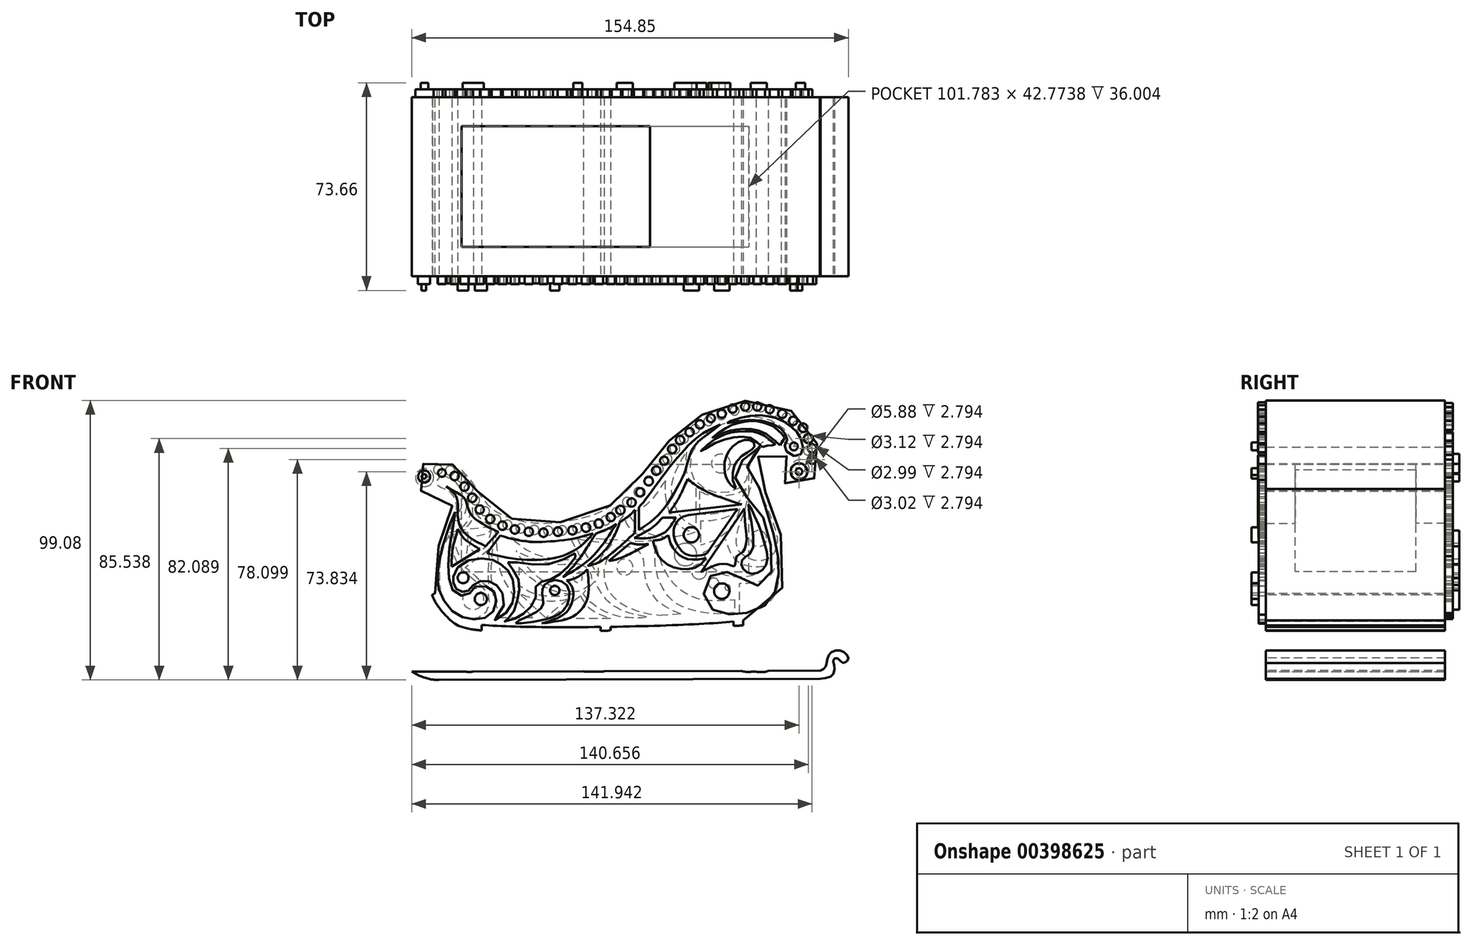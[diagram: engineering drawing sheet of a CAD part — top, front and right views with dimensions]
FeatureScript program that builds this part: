
annotation { "Feature Type Name" : "Feature", "Feature Type Description" : "" }
export const myFeature = defineFeature(function(context is Context, id is Id, definition is map)
    precondition{}
    {
        {
            var Q0;
            Q0=qCreatedBy(makeId("Front.planeOp"),FACE);
            var sketch = newSketch(context, id + "F0", { "sketchPlane" : qUnion([Q0])});
            skFitSpline(sketch, "E0", {"points": [v(-61.86, 0) * mm, v(-57.67, 0) * mm, v(-54.62, 0) * mm, v(-50.46, -2.56) * mm, v(-47.09, -6.88) * mm, v(-42.9, -13.1) * mm, v(-36.28, -18.14) * mm, v(-25.89, -20.79) * mm, v(-16.61, -20.62) * mm, v(-2.67, -17.38) * mm, v(3.41, -13.23) * mm, v(9.36, -7.64) * mm, v(15.85, 0) * mm, v(20.05, 5.35) * mm, v(25.4, 11.22) * mm, v(30.74, 15.47) * mm, v(37.88, 19.2) * mm, v(46.06, 21.92) * mm, v(55.6, 22.38) * mm, v(64.68, 19.42) * mm, v(70.58, 15.1) * mm, v(74.67, 8.3) * mm, v(75.96, 1.9) * mm, v(74.88, -3.16) * mm, v(72.79, -6.6) * mm, v(68.74, -8.77) * mm, v(63.8, -6.88) * mm, v(62.4, -3.74) * mm, v(63.54, 0) * mm, v(64.22, 2.85) * mm, v(61.07, 5.87) * mm, v(55.34, 4.34) * mm, v(53.55, 0) * mm, v(54.05, -3.2) * mm, v(57.42, -11.71) * mm, v(60.14, -18.73) * mm, v(63.09, -28.95) * mm, v(63.32, -41) * mm, v(58.78, -51.23) * mm, v(40.39, -56.22) * mm, v(-46.03, -56.8) * mm, v(-55.95, -53.28) * mm, v(-60.56, -45.22) * mm, v(-60.56, -34.78) * mm, v(-58.24, -26.54) * mm, v(-54.8, -18.71) * mm, v(-54.61, -13.18) * mm, v(-58.24, -9.36) * mm, v(-66.26, -9.17) * mm, v(-68.55, -3.06) * mm, v(-65.44, 0) * mm, v(-61.86, 0) * mm]});
            skSolve(sketch);
        }
        {
            var Q0;
            Q0 = qSketchRegion(id + "F0", true);
            extrude(context, id + "F1", {"entities" : qUnion([Q0]), "endBound" : BoundingType.SYMMETRIC, "oppositeDirection" : true, "depth" : 63.5 * mm});
        }
        {
            var Q0;
            Q0=makeQuery(id+"F1.opExtrude","CAP_FACE",FACE,{"disambiguationData":[OSD([sQuery(id+"F0.wireOp",EDGE,"E0")])],"isStart":true});
            var sketch = newSketch(context, id + "F2", { "sketchPlane" : qUnion([Q0])});
            skFitSpline(sketch, "E1.0.0", {"points": [v(-61.86, 0) * mm, v(-63.13, 0.1) * mm, v(-65.5, 0.56) * mm, v(-69.8, -2.61) * mm, v(-67.25, -11.56) * mm, v(-57.78, -7.7) * mm, v(-53.94, -13.18) * mm, v(-54.33, -18.98) * mm, v(-58.67, -26.6) * mm, v(-60.83, -34.68) * mm, v(-61.74, -45.34) * mm, v(-55.85, -54.48) * mm, v(-45.94, -58.76) * mm, v(40.55, -57.53) * mm, v(59.3, -53.74) * mm, v(64.17, -40.9) * mm, v(63.67, -29.06) * mm, v(60.18, -18.63) * mm, v(57.6, -12.08) * mm, v(53.88, -3.27) * mm, v(53.28, -0.14) * mm, v(54.58, 5.11) * mm, v(61.24, 7) * mm, v(64.98, 2.93) * mm, v(63.5, 0) * mm, v(61.9, -3.76) * mm, v(63.4, -7.3) * mm, v(68.85, -9.7) * mm, v(73.08, -6.78) * mm, v(75.06, -3.22) * mm, v(76.43, 2.03) * mm, v(75, 8.47) * mm, v(70.94, 15.58) * mm, v(64.8, 19.75) * mm, v(55.64, 23.08) * mm, v(45.99, 22.33) * mm, v(37.91, 19.4) * mm, v(30.6, 15.67) * mm, v(25.31, 11.43) * mm, v(19.88, 5.3) * mm, v(15.92, 0) * mm, v(9.53, -7.83) * mm, v(3.35, -13.28) * mm, v(-2.26, -18.21) * mm, v(-16.9, -20.96) * mm, v(-25.6, -21.2) * mm, v(-36.62, -18.82) * mm, v(-43.18, -13.54) * mm, v(-46.98, -6.86) * mm, v(-50.06, -2.48) * mm, v(-54.53, 0.48) * mm, v(-57.64, -0.1) * mm, v(-60.49, -0.12) * mm, v(-61.86, 0) * mm]});
            skLineSegment(sketch, "E2", {"start": v(-1.73, -57.73) * mm, "end": v(-1.73, -67.97) * mm});
            skLineSegment(sketch, "E3", {"start": v(1.77, -57.68) * mm, "end": v(1.77, -67.97) * mm});
            skFitSpline(sketch, "E4", {"points": [v(1.77, -67.97) * mm, v(1.77, -69.29) * mm, v(1.77, -70.2) * mm, v(1.57, -71.41) * mm, v(0.81, -72.5) * mm, v(-0.75, -73.5) * mm, v(-2.72, -73.58) * mm, v(-4.05, -73.54) * mm, v(-5.81, -73.54) * mm, v(-7.46, -73.54) * mm, v(-8.98, -72.54) * mm, v(-10.15, -70.73) * mm, v(-10.4, -68.5) * mm, v(-9.87, -67.4) * mm, v(-8.78, -66.52) * mm, v(-7.54, -66.03) * mm, v(-6.25, -66.03) * mm, v(-7.46, -67.2) * mm, v(-7.9, -69) * mm, v(-6.7, -70.45) * mm, v(-4.4, -70.85) * mm, v(-2.32, -70.09) * mm, v(-1.73, -67.97) * mm], "startDerivative": vector(-0.56, -33.67) * mm, "endDerivative": vector(1.72, 42.6) * mm});
            skLineSegment(sketch, "E5", {"start": v(45.37, -55.79) * mm, "end": v(45.37, -67.97) * mm});
            skLineSegment(sketch, "E6", {"start": v(48.81, -55.35) * mm, "end": v(48.81, -67.97) * mm});
            skFitSpline(sketch, "E7", {"points": [v(45.37, -67.97) * mm, v(45.37, -70.22) * mm, v(47.36, -72.86) * mm, v(50.54, -73.7) * mm, v(52.72, -73.58) * mm, v(56.1, -73.7) * mm, v(58.5, -72.7) * mm, v(59.86, -70.7) * mm, v(60.76, -67.97) * mm, v(60.93, -65.94) * mm, v(61.33, -64.67) * mm, v(63.14, -64.75) * mm, v(64.22, -66.01) * mm, v(63.8, -64.27) * mm, v(61.87, -63.62) * mm, v(60, -62.15) * mm, v(56.74, -62.03) * mm, v(56.33, -63.47) * mm, v(58.83, -64.44) * mm, v(59.51, -65.35) * mm, v(58.55, -69.4) * mm, v(56, -71.1) * mm, v(52.25, -71.03) * mm, v(49.75, -69.92) * mm, v(48.81, -67.97) * mm], "startDerivative": vector(-7.62, -66.67) * mm, "endDerivative": vector(-3.84, 62.66) * mm});
            skLineSegment(sketch, "E8", {"start": v(-47.46, -56.64) * mm, "end": v(-47.46, -68.5) * mm});
            skLineSegment(sketch, "E9", {"start": v(-43.88, -57) * mm, "end": v(-43.88, -68.5) * mm});
            skFitSpline(sketch, "E10", {"points": [v(-47.46, -68.5) * mm, v(-47.46, -69.9) * mm, v(-48.22, -71) * mm, v(-50.25, -71.71) * mm, v(-52.16, -71.53) * mm, v(-53.4, -70.46) * mm, v(-53.33, -68.77) * mm, v(-52.52, -67.63) * mm, v(-51.58, -66.61) * mm, v(-53.13, -66.75) * mm, v(-55.09, -68.5) * mm, v(-55.29, -71.2) * mm, v(-53.06, -73.36) * mm, v(-50.87, -73.58) * mm, v(-48.92, -73.64) * mm, v(-47.1, -73.58) * mm, v(-44.87, -72.3) * mm, v(-43.88, -68.5) * mm], "startDerivative": vector(0, -28.6) * mm, "endDerivative": vector(-5.76, 44.43) * mm});
            skLineSegment(sketch, "E11", {"start": v(76.25, -73.2) * mm, "end": v(-70.53, -73.58) * mm});
            skFitSpline(sketch, "E12", {"points": [v(-70.53, -73.58) * mm, v(-59.88, -73.36) * mm, v(-63.48, -72.42) * mm, v(-67.53, -70) * mm, v(-70.5, -66.08) * mm, v(-71.71, -60.54) * mm, v(-71.04, -55.27) * mm, v(-67.66, -50.41) * mm, v(-63.61, -47.44) * mm, v(-60.4, -45.82) * mm], "startDerivative": vector(-23.86, 1.15) * mm, "endDerivative": vector(29.7, 14.91) * mm});
            skFitSpline(sketch, "E13", {"points": [v(-60.99, -42.81) * mm, v(-62.8, -43.8) * mm, v(-64.8, -44.63) * mm, v(-66.96, -43.38) * mm, v(-69.12, -41.79) * mm, v(-73.18, -41.35) * mm, v(-74.11, -43.5) * mm, v(-71.95, -44.63) * mm, v(-69.69, -44.34) * mm, v(-67.75, -45.08) * mm, v(-66.85, -46.5) * mm, v(-70.7, -49.74) * mm, v(-74.68, -56.32) * mm, v(-74.68, -63.14) * mm, v(-73.66, -67.34) * mm, v(-71.27, -71.31) * mm, v(-66.58, -74.72) * mm, v(-61.59, -76.34) * mm, v(-59.02, -76.45) * mm], "startDerivative": vector(-40.03, -24.4) * mm, "endDerivative": vector(48.56, 3.48) * mm});
            skLineSegment(sketch, "E14", {"start": v(-59.02, -76.45) * mm, "end": v(76.08, -76.1) * mm});
            skFitSpline(sketch, "E15", {"points": [v(76.25, -73.2) * mm, v(77.38, -72.61) * mm, v(78.23, -71.53) * mm, v(78.52, -70.34) * mm, v(78.91, -68.4) * mm, v(79.7, -67.1) * mm, v(81.64, -66.08) * mm, v(83.92, -66.36) * mm, v(85.45, -67.38) * mm, v(86.13, -68.7) * mm, v(85.5, -70.06) * mm, v(84.09, -70.45) * mm, v(82.95, -69.49) * mm, v(82.04, -68.75) * mm, v(81, -69.06) * mm, v(80.8, -70.44) * mm, v(81.2, -71.89) * mm, v(80.88, -74.32) * mm, v(79.31, -75.51) * mm, v(76.08, -76.1) * mm], "startDerivative": vector(25.22, 10.43) * mm, "endDerivative": vector(-46.19, -6.72) * mm});
            skSolve(sketch);
        }
        {
            var Q0;
            {var subQ1=sQuery(id+"F2.wireOp",EDGE,"E5");Q0=makeQuery(id+"F2.imprint","IMPRINT",FACE,{"disambiguationData":[TD([[makeQuery(id+"F2.imprint","IMPRINT",EDGE,{"derivedFrom":subQ1}),1.0]])]});}
            var Q1;
            {var subQ4=sQuery(id+"F2.wireOp",EDGE,"E2");Q1=makeQuery(id+"F2.imprint","IMPRINT",FACE,{"disambiguationData":[TD([[makeQuery(id+"F2.imprint","IMPRINT",EDGE,{"derivedFrom":subQ4}),1.0]])]});}
            var Q2;
            {var subQ1=sQuery(id+"F2.wireOp",EDGE,"E8");Q2=makeQuery(id+"F2.imprint","IMPRINT",FACE,{"disambiguationData":[TD([[makeQuery(id+"F2.imprint","IMPRINT",EDGE,{"derivedFrom":subQ1}),1.0]])]});}
            var Q3;
            {var subQ11=sQuery(id+"F2.wireOp",EDGE,"E14");Q3=makeQuery(id+"F2.imprint","IMPRINT",FACE,{"disambiguationData":[TD([[makeQuery(id+"F2.imprint","IMPRINT",EDGE,{"derivedFrom":subQ11}),1.0]])]});}
            var Q4;
            {var subQ0=sQuery(id+"F2.wireOp",EDGE,"E12");var subQ1=sQuery(id+"F2.wireOp",EDGE,"E1.0.0");var subQ2=makeQuery(id+"F2.imprint","INTERSECT",VERTEX,{"derivedFrom":[subQ1,subQ0]});Q4=makeQuery(id+"F2.imprint","IMPRINT",FACE,{"disambiguationData":[TD([[makeQuery(id+"F2.imprint","IMPRINT",EDGE,{"disambiguationData":[TD([[subQ2,-1.0]])],"derivedFrom":subQ1}),1.0]])]});}
            extrude(context, id + "F3", {"entities" : qUnion([Q0, Q1, Q2, Q3, Q4]), "operationType" : NewBodyOperationType.ADD, "oppositeDirection" : true, "depth" : 63.5 * mm});
        }
        {
            var Q0;
            {var subQ0=sQuery(id+"F2.wireOp",EDGE,"E1.0.0");var subQ1=sQuery(id+"F2.wireOp",EDGE,"E11");Q0=makeQuery(id+"F3.boolean.opBoolean","MERGE",FACE,{"derivedFrom":[makeQuery(id+"F1.opExtrude","CAP_FACE",FACE,{"disambiguationData":[OSD([sQuery(id+"F0.wireOp",EDGE,"E0")])],"isStart":true}),makeQuery(id+"F3.opExtrude","CAP_FACE",FACE,{"disambiguationData":[OSD([subQ0,sQuery(id+"F2.wireOp",EDGE,"E5"),sQuery(id+"F2.wireOp",EDGE,"E6"),sQuery(id+"F2.wireOp",EDGE,"E7"),subQ1])],"isStart":true}),makeQuery(id+"F3.opExtrude","CAP_FACE",FACE,{"disambiguationData":[OSD([subQ0,sQuery(id+"F2.wireOp",EDGE,"E2"),sQuery(id+"F2.wireOp",EDGE,"E3"),sQuery(id+"F2.wireOp",EDGE,"E4"),subQ1])],"isStart":true}),makeQuery(id+"F3.opExtrude","CAP_FACE",FACE,{"disambiguationData":[OSD([subQ0,sQuery(id+"F2.wireOp",EDGE,"E8"),sQuery(id+"F2.wireOp",EDGE,"E9"),sQuery(id+"F2.wireOp",EDGE,"E10"),subQ1])],"isStart":true}),makeQuery(id+"F3.opExtrude","CAP_FACE",FACE,{"disambiguationData":[OSD([subQ0,sQuery(id+"F2.wireOp",EDGE,"E12"),sQuery(id+"F2.wireOp",EDGE,"E13")])],"isStart":true})]});}
            var sketch = newSketch(context, id + "F4", { "sketchPlane" : qUnion([Q0])});
            skCircle(sketch, "E16", {"center": v(-64.26, -4.42) * mm, "radius": 2.16 * mm});
            skCircle(sketch, "E17", {"center": v(68.61, -2.65) * mm, "radius": 2.96 * mm});
            skCircle(sketch, "E18", {"center": v(-57.99, -3.13) * mm, "radius": 1.37 * mm});
            skCircle(sketch, "E19", {"center": v(-49.97, -7.96) * mm, "radius": 1.52 * mm});
            skCircle(sketch, "E20", {"center": v(-47.2, -11.95) * mm, "radius": 1.52 * mm});
            skCircle(sketch, "E21", {"center": v(-53.47, -4.2) * mm, "radius": 1.51 * mm});
            skCircle(sketch, "E22", {"center": v(-44.56, -16.07) * mm, "radius": 1.5 * mm});
            skCircle(sketch, "E23", {"center": v(-40.84, -19.45) * mm, "radius": 1.5 * mm});
            skCircle(sketch, "E24", {"center": v(-36.51, -21.82) * mm, "radius": 1.51 * mm});
            skCircle(sketch, "E25", {"center": v(-32.1, -23.17) * mm, "radius": 1.5 * mm});
            skCircle(sketch, "E26", {"center": v(-27.17, -23.98) * mm, "radius": 1.5 * mm});
            skCircle(sketch, "E27", {"center": v(-21.95, -24.31) * mm, "radius": 1.5 * mm});
            skCircle(sketch, "E28", {"center": v(-16.84, -23.93) * mm, "radius": 1.51 * mm});
            skCircle(sketch, "E29", {"center": v(-11.67, -23.45) * mm, "radius": 1.5 * mm});
            skCircle(sketch, "E30", {"center": v(-6.9, -22.5) * mm, "radius": 1.51 * mm});
            skCircle(sketch, "E31", {"center": v(-2.38, -21.09) * mm, "radius": 1.5 * mm});
            skCircle(sketch, "E32", {"center": v(1.88, -18.77) * mm, "radius": 1.49 * mm});
            skCircle(sketch, "E33", {"center": v(5.32, -16.28) * mm, "radius": 1.53 * mm});
            skCircle(sketch, "E34", {"center": v(9.3, -13.6) * mm, "radius": 1.49 * mm});
            skCircle(sketch, "E35", {"center": v(12.35, -9.97) * mm, "radius": 1.5 * mm});
            skCircle(sketch, "E36", {"center": v(15.34, -6.05) * mm, "radius": 1.5 * mm});
            skCircle(sketch, "E37", {"center": v(18, -2.3) * mm, "radius": 1.51 * mm});
            skCircle(sketch, "E38", {"center": v(20.81, 1.23) * mm, "radius": 1.46 * mm});
            skCircle(sketch, "E39", {"center": v(23.66, 5.32) * mm, "radius": 1.5 * mm});
            skCircle(sketch, "E40", {"center": v(26.49, 8.56) * mm, "radius": 1.51 * mm});
            skCircle(sketch, "E41", {"center": v(29.82, 11.34) * mm, "radius": 1.49 * mm});
            skCircle(sketch, "E42", {"center": v(33.46, 14.13) * mm, "radius": 1.49 * mm});
            skCircle(sketch, "E43", {"center": v(37.39, 16.3) * mm, "radius": 1.45 * mm});
            skCircle(sketch, "E44", {"center": v(41.24, 17.92) * mm, "radius": 1.48 * mm});
            skCircle(sketch, "E45", {"center": v(45.1, 19.68) * mm, "radius": 1.49 * mm});
            skCircle(sketch, "E46", {"center": v(49.56, 20.42) * mm, "radius": 1.48 * mm});
            skCircle(sketch, "E47", {"center": v(53.82, 20.42) * mm, "radius": 1.46 * mm});
            skCircle(sketch, "E48", {"center": v(58.22, 19.47) * mm, "radius": 1.45 * mm});
            skCircle(sketch, "E49", {"center": v(62.68, 17.85) * mm, "radius": 1.5 * mm});
            skCircle(sketch, "E50", {"center": v(66.54, 15.35) * mm, "radius": 1.5 * mm});
            skCircle(sketch, "E51", {"center": v(70.05, 12.91) * mm, "radius": 1.51 * mm});
            skCircle(sketch, "E52", {"center": v(71.95, 9.06) * mm, "radius": 1.56 * mm});
            skCircle(sketch, "E53", {"center": v(73.23, 5.6) * mm, "radius": 1.5 * mm});
            skCircle(sketch, "E54", {"center": v(73.23, 1.62) * mm, "radius": 1.51 * mm});
            skCircle(sketch, "E55", {"center": v(68.61, -2.65) * mm, "radius": 2.94 * mm});
            skCircle(sketch, "E56", {"center": v(73.23, 1.62) * mm, "radius": 1.52 * mm});
            skCircle(sketch, "E57", {"center": v(71.95, 9.06) * mm, "radius": 1.65 * mm});
            skSolve(sketch);
        }
        {
            var Q0;
            Q0 = qSketchRegion(id + "F4", true);
            extrude(context, id + "F5", {"entities" : qUnion([Q0]), "operationType" : NewBodyOperationType.ADD, "depth" : 2.8 * mm});
        }
        {
            var Q0;
            {var subQ0=sQuery(id+"F2.wireOp",EDGE,"E1.0.0");var subQ1=sQuery(id+"F2.wireOp",EDGE,"E11");Q0=makeQuery(id+"F3.boolean.opBoolean","MERGE",FACE,{"derivedFrom":[makeQuery(id+"F1.opExtrude","CAP_FACE",FACE,{"disambiguationData":[OSD([sQuery(id+"F0.wireOp",EDGE,"E0")])],"isStart":false}),makeQuery(id+"F3.opExtrude","CAP_FACE",FACE,{"disambiguationData":[OSD([subQ0,sQuery(id+"F2.wireOp",EDGE,"E5"),sQuery(id+"F2.wireOp",EDGE,"E6"),sQuery(id+"F2.wireOp",EDGE,"E7"),subQ1])],"isStart":false}),makeQuery(id+"F3.opExtrude","CAP_FACE",FACE,{"disambiguationData":[OSD([subQ0,sQuery(id+"F2.wireOp",EDGE,"E2"),sQuery(id+"F2.wireOp",EDGE,"E3"),sQuery(id+"F2.wireOp",EDGE,"E4"),subQ1])],"isStart":false}),makeQuery(id+"F3.opExtrude","CAP_FACE",FACE,{"disambiguationData":[OSD([subQ0,sQuery(id+"F2.wireOp",EDGE,"E8"),sQuery(id+"F2.wireOp",EDGE,"E9"),sQuery(id+"F2.wireOp",EDGE,"E10"),subQ1])],"isStart":false}),makeQuery(id+"F3.opExtrude","CAP_FACE",FACE,{"disambiguationData":[OSD([subQ0,sQuery(id+"F2.wireOp",EDGE,"E12"),sQuery(id+"F2.wireOp",EDGE,"E13")])],"isStart":false})]});}
            var sketch = newSketch(context, id + "F6", { "sketchPlane" : qUnion([Q0])});
            skCircle(sketch, "E58", {"center": v(-69, -1.6) * mm, "radius": 3.2 * mm});
            skCircle(sketch, "E59", {"center": v(-71.78, 4.77) * mm, "radius": 1.56 * mm});
            skCircle(sketch, "E60", {"center": v(-70.35, 9.74) * mm, "radius": 1.54 * mm});
            skCircle(sketch, "E61", {"center": v(-67.86, 13.71) * mm, "radius": 1.56 * mm});
            skCircle(sketch, "E62", {"center": v(-64.22, 16.58) * mm, "radius": 1.56 * mm});
            skCircle(sketch, "E63", {"center": v(-59.78, 18.5) * mm, "radius": 1.6 * mm});
            skCircle(sketch, "E64", {"center": v(-55.09, 20.12) * mm, "radius": 1.53 * mm});
            skCircle(sketch, "E65", {"center": v(-50.55, 20.07) * mm, "radius": 1.56 * mm});
            skCircle(sketch, "E66", {"center": v(-45.81, 18.97) * mm, "radius": 1.58 * mm});
            skCircle(sketch, "E67", {"center": v(-41.09, 17.35) * mm, "radius": 1.57 * mm});
            skCircle(sketch, "E68", {"center": v(-36.48, 15.22) * mm, "radius": 1.57 * mm});
            skCircle(sketch, "E69", {"center": v(-31.81, 12.48) * mm, "radius": 1.58 * mm});
            skCircle(sketch, "E70", {"center": v(-27.83, 9.07) * mm, "radius": 1.58 * mm});
            skCircle(sketch, "E71", {"center": v(-24.65, 5.45) * mm, "radius": 1.76 * mm});
            skCircle(sketch, "E72", {"center": v(-21.94, 1.9) * mm, "radius": 1.67 * mm});
            skCircle(sketch, "E73", {"center": v(-18.83, -1.75) * mm, "radius": 1.68 * mm});
            skCircle(sketch, "E74", {"center": v(-15.37, -5.83) * mm, "radius": 1.65 * mm});
            skCircle(sketch, "E75", {"center": v(-11.72, -9.89) * mm, "radius": 1.63 * mm});
            skCircle(sketch, "E76", {"center": v(-7.66, -13.4) * mm, "radius": 1.63 * mm});
            skCircle(sketch, "E77", {"center": v(-3.87, -17.06) * mm, "radius": 1.6 * mm});
            skCircle(sketch, "E78", {"center": v(0, -19.96) * mm, "radius": 1.63 * mm});
            skCircle(sketch, "E79", {"center": v(4.71, -21.79) * mm, "radius": 1.59 * mm});
            skCircle(sketch, "E80", {"center": v(9.99, -22.73) * mm, "radius": 1.62 * mm});
            skCircle(sketch, "E81", {"center": v(15.33, -23.48) * mm, "radius": 1.67 * mm});
            skCircle(sketch, "E82", {"center": v(20.27, -23.62) * mm, "radius": 1.63 * mm});
            skCircle(sketch, "E83", {"center": v(25.25, -23.33) * mm, "radius": 1.64 * mm});
            skCircle(sketch, "E84", {"center": v(30.05, -22.8) * mm, "radius": 1.62 * mm});
            skCircle(sketch, "E85", {"center": v(34.72, -21.49) * mm, "radius": 1.62 * mm});
            skCircle(sketch, "E86", {"center": v(38.7, -19.67) * mm, "radius": 1.65 * mm});
            skCircle(sketch, "E87", {"center": v(42.69, -16.71) * mm, "radius": 1.59 * mm});
            skCircle(sketch, "E88", {"center": v(46.15, -12.79) * mm, "radius": 1.58 * mm});
            skCircle(sketch, "E89", {"center": v(48.54, -8.75) * mm, "radius": 1.6 * mm});
            skCircle(sketch, "E90", {"center": v(51.04, -4.76) * mm, "radius": 1.64 * mm});
            skCircle(sketch, "E91", {"center": v(55.1, -2.3) * mm, "radius": 1.65 * mm});
            skCircle(sketch, "E92", {"center": v(64.11, -4.78) * mm, "radius": 3.2 * mm});
            skCircle(sketch, "E93", {"center": v(59.35, -1.94) * mm, "radius": 1.6 * mm});
            skSolve(sketch);
        }
        {
            var Q0;
            Q0 = qSketchRegion(id + "F6", true);
            extrude(context, id + "F7", {"entities" : qUnion([Q0]), "operationType" : NewBodyOperationType.ADD, "depth" : 2.8 * mm});
        }
        {
            var Q0;
            {var subQ0=sQuery(id+"F2.wireOp",EDGE,"E6");var subQ1=sQuery(id+"F2.wireOp",EDGE,"E5");var subQ2=sQuery(id+"F0.wireOp",EDGE,"E0");var subQ3=sQuery(id+"F2.wireOp",EDGE,"E12");var subQ4=sQuery(id+"F2.wireOp",EDGE,"E4");var subQ5=sQuery(id+"F2.wireOp",EDGE,"E2");var subQ6=sQuery(id+"F2.wireOp",EDGE,"E11");var subQ8=sQuery(id+"F2.wireOp",EDGE,"E7");var subQ11=sQuery(id+"F2.wireOp",EDGE,"E8");var subQ12=sQuery(id+"F2.wireOp",EDGE,"E3");var subQ14=sQuery(id+"F2.wireOp",EDGE,"E13");var subQ15=sQuery(id+"F2.wireOp",EDGE,"E1.0.0");var subQ16=sQuery(id+"F2.wireOp",EDGE,"E9");var subQ17=sQuery(id+"F2.wireOp",EDGE,"E10");Q0=makeQuery(id+"F5.boolean.opBoolean","SPLIT",FACE,{"disambiguationData":[TD([makeQuery(id+"F1.opExtrude","SWEPT_FACE",FACE,{"disambiguationData":[OSD([subQ2])]})])],"derivedFrom":makeQuery(id+"F3.boolean.opBoolean","MERGE",FACE,{"derivedFrom":[makeQuery(id+"F1.opExtrude","CAP_FACE",FACE,{"disambiguationData":[OSD([subQ2])],"isStart":true}),makeQuery(id+"F3.opExtrude","CAP_FACE",FACE,{"disambiguationData":[OSD([subQ15,subQ1,subQ0,subQ8,subQ6])],"isStart":true}),makeQuery(id+"F3.opExtrude","CAP_FACE",FACE,{"disambiguationData":[OSD([subQ15,subQ5,subQ12,subQ4,subQ6])],"isStart":true}),makeQuery(id+"F3.opExtrude","CAP_FACE",FACE,{"disambiguationData":[OSD([subQ15,subQ11,subQ16,subQ17,subQ6])],"isStart":true}),makeQuery(id+"F3.opExtrude","CAP_FACE",FACE,{"disambiguationData":[OSD([subQ15,subQ3,subQ14])],"isStart":true})]})});}
            var sketch = newSketch(context, id + "F8", { "sketchPlane" : qUnion([Q0])});
            skFitSpline(sketch, "E94", {"points": [v(-56.44, -7.86) * mm, v(-50.71, -11.36) * mm, v(-49.16, -13.95) * mm, v(-47.8, -17.67) * mm, v(-44.9, -20.24) * mm, v(-41.28, -22.44) * mm, v(-37.95, -24) * mm], "startDerivative": vector(17.34, -13.46) * mm, "endDerivative": vector(19.44, -9.17) * mm});
            skLineSegment(sketch, "E95", {"start": v(-37.95, -24) * mm, "end": v(-42.47, -29.1) * mm});
            skFitSpline(sketch, "E96", {"points": [v(-56.44, -7.86) * mm, v(-53.05, -11.19) * mm, v(-52.3, -14.57) * mm, v(-52.36, -17.55) * mm, v(-51.96, -20.88) * mm, v(-49.2, -25.09) * mm, v(-42.47, -29.1) * mm], "startDerivative": vector(21.25, -16.5) * mm, "endDerivative": vector(32.89, -15.83) * mm});
            skFitSpline(sketch, "E97", {"points": [v(-53.23, -16.99) * mm, v(-57.76, -29.02) * mm, v(-59.45, -38.3) * mm, v(-59.25, -43.57) * mm, v(-56.64, -49.3) * mm, v(-52.45, -53.5) * mm, v(-47.58, -54.98) * mm, v(-42.98, -54.58) * mm, v(-39.82, -52.32) * mm, v(-38.67, -48.11) * mm, v(-39.62, -45.05) * mm, v(-42.97, -43.14) * mm, v(-46.7, -43.8) * mm, v(-48.23, -46) * mm, v(-51, -46.58) * mm, v(-54.45, -44.28) * mm, v(-55.56, -38.48) * mm, v(-55.26, -28.89) * mm, v(-53.23, -16.99) * mm]});
            skFitSpline(sketch, "E98", {"points": [v(-52.34, -23) * mm, v(-53.93, -28.83) * mm, v(-54.5, -34.28) * mm, v(-54.5, -36.39) * mm], "startDerivative": vector(-2.88, -14.57) * mm, "endDerivative": vector(0.26, -7.92) * mm});
            skLineSegment(sketch, "E99", {"start": v(-54.5, -36.39) * mm, "end": v(-44.56, -30.17) * mm});
            skFitSpline(sketch, "E100", {"points": [v(-52.34, -23) * mm, v(-50.49, -25.96) * mm, v(-47.81, -28.16) * mm, v(-44.56, -30.17) * mm], "startDerivative": vector(6.82, -9.23) * mm, "endDerivative": vector(9.87, -5.81) * mm});
            skFitSpline(sketch, "E101", {"points": [v(-52.34, -36.67) * mm, v(-53.88, -39.74) * mm, v(-53.99, -40.68) * mm, v(-53.96, -42.02) * mm, v(-53.3, -43.72) * mm, v(-52.17, -44.7) * mm, v(-50.86, -45.29) * mm, v(-49.61, -45.26) * mm, v(-48.47, -44.72) * mm, v(-47.5, -43.52) * mm, v(-45.7, -41.95) * mm, v(-43.34, -41.34) * mm, v(-40.9, -41.68) * mm, v(-38.74, -42.81) * mm, v(-37, -44.78) * mm, v(-35.94, -49.37) * mm, v(-38.08, -53.27) * mm, v(-39.7, -55.3) * mm, v(-36.18, -53.54) * mm, v(-33.2, -49.75) * mm, v(-32.4, -45.96) * mm, v(-32.8, -40.96) * mm, v(-34.57, -37.58) * mm, v(-36.78, -35.66) * mm, v(-38.95, -34.37) * mm, v(-42.47, -33.52) * mm, v(-47.4, -33.77) * mm, v(-52.34, -36.67) * mm]});
            skLineSegment(sketch, "E102", {"start": v(-37.26, -25.33) * mm, "end": v(-41.92, -31.53) * mm});
            skFitSpline(sketch, "E103", {"points": [v(-37.26, -25.33) * mm, v(-34.99, -26.03) * mm, v(-31.02, -26.94) * mm, v(-25.62, -27.61) * mm, v(-19.92, -27.42) * mm, v(-12.94, -26.7) * mm, v(-4.43, -24.6) * mm], "startDerivative": vector(19.1, -6.34) * mm, "endDerivative": vector(40.6, 11.48) * mm});
            skFitSpline(sketch, "E104", {"points": [v(-41.92, -31.53) * mm, v(-33.41, -33.35) * mm, v(-25.04, -33.97) * mm, v(-15.86, -32.73) * mm, v(-9.02, -29.24) * mm, v(-4.43, -24.6) * mm], "startDerivative": vector(40.97, -10.8) * mm, "endDerivative": vector(23.23, 27.39) * mm});
            skFitSpline(sketch, "E105", {"points": [v(-34.57, -34.9) * mm, v(-32.02, -38.52) * mm, v(-30.5, -43.97) * mm, v(-31.64, -49.7) * mm, v(-33.84, -54.2) * mm, v(-36.04, -55.83) * mm, v(-31.83, -54.7) * mm, v(-27.9, -52) * mm, v(-24.75, -47.7) * mm, v(-24.48, -42.88) * mm, v(-21.21, -41.39) * mm, v(-16.83, -39.53) * mm, v(-12.24, -35.13) * mm, v(-10.21, -31.63) * mm, v(-16.14, -34.3) * mm, v(-27.07, -35.42) * mm, v(-34.57, -34.9) * mm]});
            skFitSpline(sketch, "E106", {"points": [v(-31.83, -56.37) * mm, v(-26.05, -53.26) * mm, v(-22.23, -50.1) * mm, v(-22.26, -47.04) * mm, v(-22.4, -44.74) * mm, v(-21.23, -42.45) * mm, v(-17.2, -41.11) * mm, v(-13.22, -43.73) * mm, v(-13.34, -49.34) * mm, v(-15.77, -52.58) * mm, v(-19.94, -54.7) * mm, v(-31.83, -56.37) * mm]});
            skFitSpline(sketch, "E107", {"points": [v(-15.06, -40.04) * mm, v(-9.83, -34.35) * mm, v(-6.7, -29.86) * mm, v(-3.46, -24.68) * mm], "startDerivative": vector(15.46, 15.9) * mm, "endDerivative": vector(10.16, 16.32) * mm});
            skFitSpline(sketch, "E108", {"points": [v(-3.46, -24.68) * mm, v(-1.24, -23.77) * mm, v(1.6, -22.58) * mm, v(3.88, -21.16) * mm], "startDerivative": vector(6.77, 2.85) * mm, "endDerivative": vector(6.5, 4.5) * mm});
            skFitSpline(sketch, "E109", {"points": [v(3.88, -21.16) * mm, v(-4.76, -32.93) * mm, v(-15.06, -40.04) * mm], "startDerivative": vector(-15.4, -24.71) * mm, "endDerivative": vector(-22.56, -12.9) * mm});
            skFitSpline(sketch, "E110", {"points": [v(-22.59, -56.49) * mm, v(-17.23, -54.72) * mm, v(-13.55, -52.13) * mm, v(-11.54, -47.83) * mm, v(-11.73, -44) * mm, v(-13.02, -41.8) * mm, v(-13.79, -41.28) * mm], "startDerivative": vector(26.39, 7.47) * mm, "endDerivative": vector(-8.58, 4.5) * mm});
            skFitSpline(sketch, "E111", {"points": [v(-13.79, -41.28) * mm, v(-11.2, -40.66) * mm, v(-7.86, -38.7) * mm, v(-6.47, -37.3) * mm], "startDerivative": vector(7.53, 1.15) * mm, "endDerivative": vector(4.12, 4.76) * mm});
            skFitSpline(sketch, "E112", {"points": [v(-6.47, -37.3) * mm, v(-6.04, -40.6) * mm, v(-6.04, -45.72) * mm, v(-6.95, -49.26) * mm, v(-9.63, -52.66) * mm, v(-13.54, -54.86) * mm, v(-22.59, -56.49) * mm], "startDerivative": vector(3.28, -22.1) * mm, "endDerivative": vector(-43.28, -5.66) * mm});
            skFitSpline(sketch, "E113", {"points": [v(54.82, 6.19) * mm, v(50.23, -0.7) * mm, v(54.25, -7.97) * mm, v(57.14, -16.25) * mm, v(59.44, -24.23) * mm, v(60.92, -31.13) * mm, v(61.46, -36.14) * mm, v(61.2, -40.74) * mm, v(60.11, -45.2) * mm, v(58.22, -48.58) * mm, v(53.62, -51.7) * mm, v(48.61, -53.05) * mm, v(44.42, -53.32) * mm, v(40.36, -52.5) * mm, v(36.55, -50.53) * mm, v(34.83, -45.18) * mm, v(36.74, -40.1) * mm, v(41.14, -38.3) * mm, v(44.2, -38.39) * mm, v(47.53, -39.8) * mm, v(51.18, -42.9) * mm, v(56.45, -41.92) * mm, v(59.22, -36.47) * mm, v(57.88, -25.38) * mm, v(53.86, -15.43) * mm, v(47.65, -9.21) * mm, v(46.02, -2.7) * mm, v(49.43, 2.14) * mm, v(54.82, 6.19) * mm]});
            skFitSpline(sketch, "E114", {"points": [v(66.85, 2.92) * mm, v(69.36, 3.67) * mm, v(70.05, 6.65) * mm, v(68.5, 10.5) * mm, v(66.68, 12.5) * mm, v(63.23, 15.16) * mm, v(59.45, 16.6) * mm, v(56.05, 17.27) * mm, v(51, 17.1) * mm, v(46.12, 15.85) * mm, v(43.06, 14.6) * mm, v(48.13, 15.37) * mm, v(55.29, 15.45) * mm, v(61.61, 13.07) * mm, v(63.43, 11.16) * mm, v(64.48, 9.15) * mm, v(63.7, 7) * mm, v(63.8, 5.08) * mm, v(66.85, 2.92) * mm]});
            skLineSegment(sketch, "E115", {"start": v(63.54, 9.39) * mm, "end": v(61.93, 6.73) * mm});
            skFitSpline(sketch, "E116", {"points": [v(63.54, 9.39) * mm, v(62.09, 11.16) * mm, v(59.63, 13.26) * mm, v(57.67, 14.17) * mm, v(54.45, 15.05) * mm, v(51.04, 15.28) * mm, v(46.5, 14.48) * mm, v(42.65, 12.75) * mm, v(37.96, 9.39) * mm, v(41.46, 10.93) * mm, v(45.76, 12.2) * mm, v(50.67, 12.53) * mm, v(55.9, 11.32) * mm, v(61.93, 6.73) * mm], "startDerivative": vector(-21.37, 30.93) * mm, "endDerivative": vector(57.36, -51.2) * mm});
            skFitSpline(sketch, "E117", {"points": [v(55.74, 6) * mm, v(57.12, 6.48) * mm, v(58.94, 6.77) * mm, v(60.33, 6.72) * mm, v(58.37, 8.59) * mm, v(56.55, 9.97) * mm, v(53.68, 11.22) * mm, v(51, 11.7) * mm, v(47.32, 11.6) * mm, v(44.54, 11.27) * mm, v(42.14, 10.5) * mm, v(40.01, 9.48) * mm, v(37.61, 8.06) * mm, v(33.83, 4.57) * mm, v(37.47, 6.72) * mm, v(43.7, 9.17) * mm, v(48.8, 9.69) * mm, v(52.68, 8.68) * mm, v(55.74, 6) * mm]});
            skFitSpline(sketch, "E118", {"points": [v(51.03, 8.57) * mm, v(52.5, 7.77) * mm, v(52.85, 6.24) * mm, v(52, 5.21) * mm, v(49.5, 3.68) * mm, v(46.65, 1.12) * mm, v(45.34, -1.72) * mm, v(45.34, -6.39) * mm, v(46.3, -8.78) * mm, v(45.11, -7.92) * mm, v(43.92, -6.84) * mm, v(43.12, -5.42) * mm, v(42.44, -3.72) * mm, v(42.21, -1.38) * mm, v(42.38, 1.35) * mm, v(43.46, 4.13) * mm, v(45.4, 6.58) * mm, v(48.92, 8.57) * mm, v(51.03, 8.57) * mm]});
            skFitSpline(sketch, "E119", {"points": [v(45.47, 8.2) * mm, v(43.27, 6.28) * mm, v(41.36, 2.55) * mm, v(40.88, -2.7) * mm, v(42.12, -6.91) * mm, v(45.66, -10.26) * mm, v(48.05, -11.41) * mm], "startDerivative": vector(-16.05, -11.76) * mm, "endDerivative": vector(16.58, -6.5) * mm});
            skFitSpline(sketch, "E120", {"points": [v(45.28, 8.2) * mm, v(42.12, 7.72) * mm, v(38.72, 6.46) * mm, v(34.47, 3.9) * mm, v(31.31, 1.4) * mm, v(30.2, -2.88) * mm, v(48.05, -11.41) * mm], "startDerivative": vector(-26, -1.56) * mm, "endDerivative": vector(91, -32.87) * mm});
            skFitSpline(sketch, "E121", {"points": [v(40.65, 14.04) * mm, v(33.83, 10.4) * mm, v(28.14, 5.29) * mm, v(21.1, -3.25) * mm, v(14.72, -11.9) * mm, v(11.88, -15.3) * mm], "startDerivative": vector(-36.56, -17.17) * mm, "endDerivative": vector(-17.61, -20.07) * mm});
            skLineSegment(sketch, "E122", {"start": v(11.88, -15.3) * mm, "end": v(11.88, -23.38) * mm});
            skFitSpline(sketch, "E123", {"points": [v(11.88, -23.38) * mm, v(19.04, -17.8) * mm, v(24.73, -9.62) * mm, v(28.03, -3.13) * mm, v(29.4, 1.76) * mm, v(32.34, 7.38) * mm, v(40.65, 14.04) * mm], "startDerivative": vector(42.16, 27.67) * mm, "endDerivative": vector(43.8, 40.17) * mm});
            skFitSpline(sketch, "E124", {"points": [v(29.14, -5.3) * mm, v(25.6, -12.7) * mm, v(22.54, -17.2) * mm], "startDerivative": vector(-6.32, -14.36) * mm, "endDerivative": vector(-6.9, -9.27) * mm});
            skLineSegment(sketch, "E125", {"start": v(22.54, -17.2) * mm, "end": v(48.28, -14.3) * mm});
            skFitSpline(sketch, "E126", {"points": [v(29.14, -5.3) * mm, v(35.09, -9.32) * mm, v(48.28, -14.3) * mm], "startDerivative": vector(12.56, -9.89) * mm, "endDerivative": vector(25.03, -8.22) * mm});
            skFitSpline(sketch, "E127", {"points": [v(50.7, -14.3) * mm, v(54.23, -21.54) * mm, v(56.48, -28.3) * mm, v(57.29, -34.57) * mm, v(54.23, -38.43) * mm, v(50.23, -38.37) * mm, v(48.28, -35.86) * mm, v(48.81, -33.48) * mm, v(52.3, -30.07) * mm, v(50.7, -14.3) * mm]});
            skFitSpline(sketch, "E128", {"points": [v(49.17, -15.73) * mm, v(49.74, -22.9) * mm, v(50.02, -26.97) * mm, v(48.67, -31.16) * mm, v(46.32, -33.02) * mm, v(45.87, -36.09) * mm, v(44.05, -35.75) * mm, v(40.25, -35.5) * mm, v(37.1, -36.66) * mm, v(33.8, -38.42) * mm], "startDerivative": vector(4.78, -49.6) * mm, "endDerivative": vector(-23.8, -23.06) * mm});
            skLineSegment(sketch, "E129", {"start": v(49.17, -15.73) * mm, "end": v(33.8, -38.42) * mm});
            skLineSegment(sketch, "E130", {"start": v(46.85, -15.86) * mm, "end": v(36.15, -31.44) * mm});
            skLineSegment(sketch, "E131", {"start": v(46.85, -15.86) * mm, "end": v(29.46, -18.03) * mm});
            skFitSpline(sketch, "E132", {"points": [v(29.46, -18.03) * mm, v(26.83, -19.04) * mm, v(24.72, -21.5) * mm, v(24.13, -24.16) * mm, v(25.2, -28.14) * mm, v(29.46, -32.26) * mm, v(35.13, -32.02) * mm, v(36.15, -31.44) * mm], "startDerivative": vector(-21.82, -4.59) * mm, "endDerivative": vector(16.27, 12.25) * mm});
            skLineSegment(sketch, "E133", {"start": v(20.2, -19.02) * mm, "end": v(25.07, -19.02) * mm});
            skLineSegment(sketch, "E134", {"start": v(20.2, -19.02) * mm, "end": v(18, -21.41) * mm});
            skLineSegment(sketch, "E135", {"start": v(18, -21.41) * mm, "end": v(15.92, -23.07) * mm});
            skLineSegment(sketch, "E136", {"start": v(15.92, -23.07) * mm, "end": v(10.24, -26.2) * mm});
            skFitSpline(sketch, "E137", {"points": [v(25.07, -19.02) * mm, v(23.44, -21.41) * mm, v(21.15, -24.09) * mm, v(15.4, -26.2) * mm, v(10.24, -26.2) * mm], "startDerivative": vector(-7.94, -11.49) * mm, "endDerivative": vector(-18.14, 1.46) * mm});
            skFitSpline(sketch, "E138", {"points": [v(16.87, -27.08) * mm, v(19.93, -26.6) * mm, v(22.34, -25.15) * mm], "startDerivative": vector(6.23, 0.43) * mm, "endDerivative": vector(4.7, 3.46) * mm});
            skFitSpline(sketch, "E139", {"points": [v(5.13, -20.53) * mm, v(8.11, -18.5) * mm, v(10.4, -16.27) * mm], "startDerivative": vector(6.05, 3.77) * mm, "endDerivative": vector(4.48, 4.76) * mm});
            skFitSpline(sketch, "E140", {"points": [v(10.4, -16.27) * mm, v(10.4, -18.64) * mm, v(10.4, -21.48) * mm, v(10.4, -24.32) * mm], "startDerivative": vector(0, -7.37) * mm, "endDerivative": vector(0, -8.22) * mm});
            skFitSpline(sketch, "E141", {"points": [v(5.13, -20.53) * mm, v(3.7, -24.19) * mm, v(0, -30.3) * mm, v(-6.24, -36.05) * mm], "startDerivative": vector(-4.63, -13.06) * mm, "endDerivative": vector(-17.43, -13.97) * mm});
            skFitSpline(sketch, "E142", {"points": [v(-6.24, -36.05) * mm, v(-1.46, -34.33) * mm, v(10.4, -24.32) * mm], "startDerivative": vector(12.14, 2.73) * mm, "endDerivative": vector(20.42, 19.23) * mm});
            skFitSpline(sketch, "E143", {"points": [v(22.34, -25.15) * mm, v(23.22, -28.4) * mm, v(25.8, -31.94) * mm, v(29.24, -33.66) * mm, v(33.93, -33.66) * mm, v(35.46, -33.37) * mm, v(32.69, -36.24) * mm, v(23.98, -36.53) * mm, v(18.72, -32.41) * mm, v(16.87, -27.08) * mm], "startDerivative": vector(5.97, -33.55) * mm, "endDerivative": vector(-10.2, 44.97) * mm});
            skFitSpline(sketch, "E144", {"points": [v(8.87, -27.92) * mm, v(11.83, -28.5) * mm, v(15.28, -28.3) * mm], "startDerivative": vector(6, -1.56) * mm, "endDerivative": vector(6.8, 0.77) * mm});
            skFitSpline(sketch, "E145", {"points": [v(8.87, -27.92) * mm, v(1.21, -34.33) * mm], "startDerivative": vector(-7.66, -6.4) * mm, "endDerivative": vector(-7.66, -6.4) * mm});
            skFitSpline(sketch, "E146", {"points": [v(1.21, -34.33) * mm, v(5.14, -33.37) * mm, v(15.28, -28.3) * mm], "startDerivative": vector(9.44, 1.52) * mm, "endDerivative": vector(17.97, 9.83) * mm});
            skSolve(sketch);
        }
        {
            var Q0;
            Q0 = qSketchRegion(id + "F8", true);
            extrude(context, id + "F9", {"entities" : qUnion([Q0]), "operationType" : NewBodyOperationType.ADD, "depth" : 2.54 * mm});
        }
        {
            var Q0;
            {var subQ0=sQuery(id+"F2.wireOp",EDGE,"E1.0.0");var subQ1=sQuery(id+"F2.wireOp",EDGE,"E11");Q0=makeQuery(id+"F3.boolean.opBoolean","MERGE",FACE,{"derivedFrom":[makeQuery(id+"F1.opExtrude","CAP_FACE",FACE,{"disambiguationData":[OSD([sQuery(id+"F0.wireOp",EDGE,"E0")])],"isStart":false}),makeQuery(id+"F3.opExtrude","CAP_FACE",FACE,{"disambiguationData":[OSD([subQ0,sQuery(id+"F2.wireOp",EDGE,"E5"),sQuery(id+"F2.wireOp",EDGE,"E6"),sQuery(id+"F2.wireOp",EDGE,"E7"),subQ1])],"isStart":false}),makeQuery(id+"F3.opExtrude","CAP_FACE",FACE,{"disambiguationData":[OSD([subQ0,sQuery(id+"F2.wireOp",EDGE,"E2"),sQuery(id+"F2.wireOp",EDGE,"E3"),sQuery(id+"F2.wireOp",EDGE,"E4"),subQ1])],"isStart":false}),makeQuery(id+"F3.opExtrude","CAP_FACE",FACE,{"disambiguationData":[OSD([subQ0,sQuery(id+"F2.wireOp",EDGE,"E8"),sQuery(id+"F2.wireOp",EDGE,"E9"),sQuery(id+"F2.wireOp",EDGE,"E10"),subQ1])],"isStart":false}),makeQuery(id+"F3.opExtrude","CAP_FACE",FACE,{"disambiguationData":[OSD([subQ0,sQuery(id+"F2.wireOp",EDGE,"E12"),sQuery(id+"F2.wireOp",EDGE,"E13")])],"isStart":false})]});}
            var sketch = newSketch(context, id + "F10", { "sketchPlane" : qUnion([Q0])});
            skFitSpline(sketch, "E147", {"points": [v(-66.4, 8.2) * mm, v(-63.62, 12.17) * mm, v(-59.12, 15.3) * mm, v(-55.3, 16.5) * mm, v(-50.7, 16.66) * mm, v(-46.43, 15.92) * mm, v(-43.08, 14.84) * mm, v(-39.44, 13.25) * mm, v(-35.75, 10.75) * mm, v(-33.7, 8.93) * mm, v(-31.2, 5.69) * mm, v(-29.94, 0.63) * mm, v(-30.28, -3.18) * mm, v(-31.59, -5.57) * mm, v(-34.44, -8.19) * mm, v(-37.28, -9.73) * mm, v(-41.44, -10) * mm, v(-45.08, -9.5) * mm, v(-47.97, -8.08) * mm, v(-49.63, -6.14) * mm, v(-50.42, -4.55) * mm, v(-50.82, -1.82) * mm, v(-51.28, 0.63) * mm, v(-52.07, 2.9) * mm, v(-52.87, 4.66) * mm, v(-54.46, 6.75) * mm, v(-56.55, 8.28) * mm, v(-58.56, 8.6) * mm, v(-60.37, 8.68) * mm, v(-62.3, 8.36) * mm, v(-67.37, 6.2) * mm], "startDerivative": vector(67.96, 101.36) * mm, "endDerivative": vector(-135.96, -63.5) * mm});
            skLineSegment(sketch, "E148", {"start": v(-66.4, 8.2) * mm, "end": v(-67.37, 6.2) * mm});
            skFitSpline(sketch, "E149", {"points": [v(-52.15, -3.8) * mm, v(-54.97, -10.24) * mm, v(-57.67, -16.45) * mm, v(-59.55, -21.26) * mm, v(-61, -27.7) * mm, v(-58.9, -32.68) * mm, v(-54.02, -34.31) * mm, v(-47.61, -31.33) * mm, v(-46.4, -25.54) * mm, v(-48.01, -20.31) * mm, v(-49.38, -16.37) * mm, v(-51.23, -8.9) * mm], "startDerivative": vector(-29.54, -62.86) * mm, "endDerivative": vector(-20, 83.44) * mm});
            skLineSegment(sketch, "E150", {"start": v(-52.15, -3.8) * mm, "end": v(-51.23, -8.9) * mm});
            skFitSpline(sketch, "E151", {"points": [v(-49.86, -8.73) * mm, v(-46.24, -10.5) * mm, v(-41.58, -11.39) * mm, v(-37.07, -11.14) * mm, v(-33.3, -9.54) * mm], "startDerivative": vector(15.25, -11.12) * mm, "endDerivative": vector(15.05, 8.11) * mm});
            skLineSegment(sketch, "E152", {"start": v(-33.3, -9.54) * mm, "end": v(-33.3, -17.66) * mm});
            skFitSpline(sketch, "E153", {"points": [v(-49.86, -8.73) * mm, v(-48.01, -12.35) * mm, v(-44, -16.13) * mm, v(-37.15, -17.82) * mm, v(-33.3, -17.66) * mm], "startDerivative": vector(6.3, -16.7) * mm, "endDerivative": vector(16.47, 2.35) * mm});
            skFitSpline(sketch, "E154", {"points": [v(-28.7, 4.3) * mm, v(-28.55, -1.57) * mm, v(-29.84, -5.6) * mm, v(-32.09, -8.65) * mm], "startDerivative": vector(1.46, -16.25) * mm, "endDerivative": vector(-8.04, -9.61) * mm});
            skLineSegment(sketch, "E155", {"start": v(-32.09, -8.65) * mm, "end": v(-32.09, -22.4) * mm});
            skFitSpline(sketch, "E156", {"points": [v(-32.09, -22.4) * mm, v(-27.34, -19.35) * mm, v(-23.72, -11.7) * mm, v(-24.2, -4.39) * mm, v(-28.7, 4.3) * mm], "startDerivative": vector(24.48, 10.34) * mm, "endDerivative": vector(-20.4, 31.4) * mm});
            skFitSpline(sketch, "E157", {"points": [v(-47.61, -15.84) * mm, v(-44.43, -18.12) * mm, v(-39.76, -19.7) * mm, v(-35.67, -20.16) * mm, v(-33.74, -20.16) * mm], "startDerivative": vector(11.37, -9.37) * mm, "endDerivative": vector(9.64, 0.21) * mm});
            skLineSegment(sketch, "E158", {"start": v(-33.74, -20.16) * mm, "end": v(-33.74, -28.7) * mm});
            skFitSpline(sketch, "E159", {"points": [v(-47.61, -15.84) * mm, v(-45.68, -20.5) * mm, v(-40.56, -25.97) * mm, v(-33.74, -28.7) * mm], "startDerivative": vector(5.04, -15.66) * mm, "endDerivative": vector(20.13, -5.76) * mm});
            skPoint(sketch, "E160.5.internal.snap0", {"position": v(-48.81, -61.66) * mm});
            skFitSpline(sketch, "E160", {"points": [v(-61.41, -32.68) * mm, v(-61.55, -39.14) * mm, v(-60.47, -45.1) * mm, v(-57.5, -49.43) * mm, v(-52.87, -52) * mm, v(-48.81, -52.8) * mm, v(-47.61, -52.8) * mm], "startDerivative": vector(-1.73, -32.42) * mm, "endDerivative": vector(11.87, 0.63) * mm});
            skLineSegment(sketch, "E161", {"start": v(-47.61, -52.8) * mm, "end": v(-47.61, -42.4) * mm});
            skFitSpline(sketch, "E162", {"points": [v(-61.41, -32.68) * mm, v(-59.25, -38.2) * mm, v(-55.33, -41.44) * mm, v(-47.61, -42.4) * mm], "startDerivative": vector(5.38, -18.15) * mm, "endDerivative": vector(22.5, -0.57) * mm});
            skFitSpline(sketch, "E163", {"points": [v(-56.42, -36.35) * mm, v(-52.9, -39.19) * mm, v(-46, -40) * mm, v(-41, -38.78) * mm, v(-37.07, -35.67) * mm, v(-34.64, -31.34) * mm], "startDerivative": vector(16.06, -17.7) * mm, "endDerivative": vector(10.76, 23.45) * mm});
            skFitSpline(sketch, "E164", {"points": [v(-34.64, -31.34) * mm, v(-38.02, -29.72) * mm, v(-40.7, -28.2) * mm, v(-42.62, -26.74) * mm], "startDerivative": vector(-9.2, 4.8) * mm, "endDerivative": vector(-5.25, 6.49) * mm});
            skFitSpline(sketch, "E165", {"points": [v(-56.42, -36.35) * mm, v(-51.95, -36.35) * mm, v(-46.4, -34.18) * mm, v(-42.62, -26.74) * mm], "startDerivative": vector(15.02, -0.92) * mm, "endDerivative": vector(7.6, 22.28) * mm});
            skPoint(sketch, "E166.2.internal.snap0", {"position": v(-33.3, -13.6) * mm});
            skFitSpline(sketch, "E166", {"points": [v(-21.22, -5.9) * mm, v(-21.13, -9.63) * mm, v(-21.6, -13.6) * mm, v(-23.72, -19.1) * mm, v(-28.3, -23.12) * mm, v(-31.74, -24.17) * mm], "startDerivative": vector(1.1, -20.81) * mm, "endDerivative": vector(-18.8, -3.73) * mm});
            skFitSpline(sketch, "E167", {"points": [v(-21.22, -5.9) * mm, v(-18.45, -9.92) * mm, v(-15.1, -13.84) * mm, v(-11.08, -16.61) * mm, v(-8.02, -17.66) * mm], "startDerivative": vector(12.01, -14.7) * mm, "endDerivative": vector(14.23, -3.61) * mm});
            skFitSpline(sketch, "E168", {"points": [v(-31.74, -24.17) * mm, v(-28.3, -25.13) * mm, v(-21.6, -25.9) * mm, v(-14.53, -24.17) * mm, v(-8.02, -17.66) * mm], "startDerivative": vector(16.63, -6.34) * mm, "endDerivative": vector(20.84, 26.89) * mm});
            skLineSegment(sketch, "E169", {"start": v(-45.83, -49.81) * mm, "end": v(-45.83, -52.57) * mm});
            skFitSpline(sketch, "E170", {"points": [v(-45.83, -52.57) * mm, v(-40.74, -53.06) * mm, v(-31.8, -52.07) * mm, v(-24.01, -48.6) * mm, v(-19.91, -43.25) * mm, v(-18.02, -37.85) * mm, v(-17.54, -32.3) * mm, v(-17.88, -28.71) * mm], "startDerivative": vector(36.2, -5.47) * mm, "endDerivative": vector(-2.5, 35.9) * mm});
            skFitSpline(sketch, "E171", {"points": [v(-17.88, -28.71) * mm, v(-19.35, -33.8) * mm, v(-21.96, -39.44) * mm, v(-26.29, -44.27) * mm, v(-32.14, -47.4) * mm, v(-38.3, -48.33) * mm, v(-45.83, -48.06) * mm], "startDerivative": vector(-7.34, -32.1) * mm, "endDerivative": vector(-42.97, 2.4) * mm});
            skFitSpline(sketch, "E172", {"points": [v(-45.83, -48.06) * mm, v(-45.83, -49.81) * mm], "startDerivative": vector(0, -1.76) * mm, "endDerivative": vector(0, -1.76) * mm});
            skFitSpline(sketch, "E173", {"points": [v(-16.45, -27.15) * mm, v(-12.43, -25.47) * mm, v(-9.24, -23.22) * mm, v(-7.25, -20.52) * mm, v(-6.34, -18.22) * mm, v(-4.54, -20.92) * mm, v(-2.53, -22.8) * mm, v(1.68, -24.3) * mm, v(4.8, -24.85) * mm, v(8.71, -25.52) * mm, v(-16.45, -27.15) * mm]});
            skFitSpline(sketch, "E174", {"points": [v(-26.75, -53.12) * mm, v(-21.44, -50.7) * mm, v(-16.61, -46.36) * mm, v(-14.04, -39.76) * mm, v(-13.72, -34.77) * mm, v(-11.3, -30.43) * mm, v(-6.75, -29.2) * mm, v(-3.26, -30.43) * mm, v(0, -35.1) * mm, v(0, -42.82) * mm, v(-4.55, -48.66) * mm, v(-9.86, -51.5) * mm, v(-19.76, -53.63) * mm], "startDerivative": vector(65.94, 25.8) * mm, "endDerivative": vector(-96.44, -3.78) * mm});
            skLineSegment(sketch, "E175", {"start": v(-26.75, -53.12) * mm, "end": v(-19.76, -53.63) * mm});
            skLineSegment(sketch, "E176", {"start": v(-2.16, -28.32) * mm, "end": v(9.9, -26.73) * mm});
            skLineSegment(sketch, "E177", {"start": v(-2.16, -28.32) * mm, "end": v(1.14, -32.42) * mm});
            skFitSpline(sketch, "E178", {"points": [v(1.14, -32.42) * mm, v(2, -34.18) * mm, v(2.64, -37) * mm, v(2.56, -39.73) * mm], "startDerivative": vector(3.06, -5.52) * mm, "endDerivative": vector(-0.69, -7.72) * mm});
            skLineSegment(sketch, "E179", {"start": v(9.9, -26.73) * mm, "end": v(2.56, -39.73) * mm});
            skFitSpline(sketch, "E180", {"points": [v(-14.5, -54.12) * mm, v(-7.98, -52.68) * mm, v(-3.87, -50.83) * mm, v(-0.74, -48.5) * mm, v(2.4, -44.15) * mm, v(3.69, -41.5) * mm], "startDerivative": vector(28.58, 5.12) * mm, "endDerivative": vector(6.65, 15.28) * mm});
            skLineSegment(sketch, "E181", {"start": v(3.69, -41.5) * mm, "end": v(7.95, -45.84) * mm});
            skFitSpline(sketch, "E182", {"points": [v(-14.5, -54.12) * mm, v(-11.11, -54.53) * mm, v(-4.36, -53.88) * mm, v(3.44, -50.34) * mm, v(7.95, -45.84) * mm], "startDerivative": vector(13.05, -6.11) * mm, "endDerivative": vector(14.18, 19.86) * mm});
            skFitSpline(sketch, "E183", {"points": [v(12.25, -26.54) * mm, v(18.18, -27.3) * mm, v(26.79, -27.3) * mm, v(33.3, -25.96) * mm], "startDerivative": vector(18.1, -2.83) * mm, "endDerivative": vector(18.98, 5) * mm});
            skLineSegment(sketch, "E184", {"start": v(12.25, -26.54) * mm, "end": v(8.42, -33.8) * mm});
            skFitSpline(sketch, "E185", {"points": [v(8.42, -33.8) * mm, v(16.75, -33.8) * mm, v(26.02, -31.42) * mm, v(33.3, -25.96) * mm], "startDerivative": vector(25.11, -0.5) * mm, "endDerivative": vector(18.26, 21.11) * mm});
            skPoint(sketch, "E186.8.internal.snap0", {"position": v(6.23, -33.23) * mm});
            skFitSpline(sketch, "E186", {"points": [v(9.38, -35.53) * mm, v(7.08, -36.39) * mm, v(5.08, -39.26) * mm, v(5.55, -42.32) * mm, v(9.86, -45.19) * mm, v(17.7, -43.95) * mm, v(21.81, -41.65) * mm, v(26.6, -37.63) * mm, v(30.14, -33.23) * mm, v(31.57, -30.75) * mm], "startDerivative": vector(-27.03, -6.76) * mm, "endDerivative": vector(13.85, 25.63) * mm});
            skFitSpline(sketch, "E187", {"points": [v(9.38, -35.53) * mm, v(12.63, -35.53) * mm, v(17.9, -35.53) * mm, v(28.32, -32.47) * mm, v(31.57, -30.75) * mm], "startDerivative": vector(16.38, 0.46) * mm, "endDerivative": vector(12.56, 7.75) * mm});
            skFitSpline(sketch, "E188", {"points": [v(8.8, -46.82) * mm, v(7.47, -49.11) * mm, v(3.74, -52.36) * mm, v(-1.81, -54.75) * mm], "startDerivative": vector(-4.16, -8.65) * mm, "endDerivative": vector(-14.84, -5.24) * mm});
            skLineSegment(sketch, "E189", {"start": v(-1.81, -54.75) * mm, "end": v(19.61, -54.75) * mm});
            skFitSpline(sketch, "E190", {"points": [v(8.8, -46.82) * mm, v(19.61, -54.75) * mm], "startDerivative": vector(10.8, -7.94) * mm, "endDerivative": vector(10.8, -7.94) * mm});
            skFitSpline(sketch, "E191", {"points": [v(11.65, -46.1) * mm, v(16.01, -45.64) * mm, v(23.28, -42.6) * mm, v(28.7, -38.47) * mm, v(30.72, -36.44) * mm], "startDerivative": vector(17.93, 0.61) * mm, "endDerivative": vector(9.64, 10.14) * mm});
            skLineSegment(sketch, "E192", {"start": v(30.72, -36.44) * mm, "end": v(30.72, -43) * mm});
            skFitSpline(sketch, "E193", {"points": [v(11.65, -46.1) * mm, v(16.25, -46.85) * mm, v(24.77, -46.1) * mm, v(30.72, -43) * mm], "startDerivative": vector(14.68, -3.26) * mm, "endDerivative": vector(15.98, 10.72) * mm});
            skFitSpline(sketch, "E194", {"points": [v(13.2, -47.94) * mm, v(16.02, -50.2) * mm, v(18.91, -52.52) * mm, v(20.68, -54.21) * mm, v(21.09, -54.54) * mm], "startDerivative": vector(8.94, -7.25) * mm, "endDerivative": vector(2.92, -2.11) * mm});
            skFitSpline(sketch, "E195", {"points": [v(13.2, -47.94) * mm, v(18.67, -48.66) * mm, v(24.38, -47.94) * mm, v(29.93, -46.1) * mm, v(31.3, -45.19) * mm], "startDerivative": vector(19.75, -3.69) * mm, "endDerivative": vector(7.07, 5.86) * mm});
            skLineSegment(sketch, "E196", {"start": v(21.09, -54.54) * mm, "end": v(31.3, -45.19) * mm});
            skFitSpline(sketch, "E197", {"points": [v(55.4, -25.13) * mm, v(57.3, -29.18) * mm, v(58.51, -33.65) * mm, v(58.92, -39.33) * mm, v(58.51, -45.42) * mm, v(56.75, -49.2) * mm, v(54.32, -51.9) * mm, v(51.75, -53.8) * mm, v(48.37, -54.89) * mm, v(44.3, -53.94) * mm, v(41.35, -50.9) * mm, v(41.38, -46.36) * mm, v(44.44, -42.85) * mm, v(47.29, -40.55) * mm, v(50.26, -37.84) * mm, v(53.5, -33.1) * mm, v(54.86, -27.83) * mm, v(55.4, -25.13) * mm]});
            skLineSegment(sketch, "E198", {"start": v(25.7, -54.54) * mm, "end": v(37.2, -54.54) * mm});
            skFitSpline(sketch, "E199", {"points": [v(25.7, -54.54) * mm, v(30.3, -49.4) * mm, v(33.15, -45.62) * mm, v(36.22, -40.47) * mm, v(38.02, -33.71) * mm, v(39.24, -23.3) * mm, v(40.32, -32.36) * mm, v(40.57, -37.66) * mm, v(40.05, -45.48) * mm, v(37.2, -54.54) * mm], "startDerivative": vector(45.6, 49.66) * mm, "endDerivative": vector(-25.72, -76.7) * mm});
            skFitSpline(sketch, "E200", {"points": [v(41.22, -30.32) * mm, v(41.38, -34.18) * mm, v(41.62, -40.86) * mm, v(41.22, -44) * mm], "startDerivative": vector(0.36, -11.14) * mm, "endDerivative": vector(-1.89, -9.76) * mm});
            skFitSpline(sketch, "E201", {"points": [v(41.22, -44) * mm, v(44.35, -41.34) * mm, v(46.77, -39.1) * mm, v(49.66, -36.68) * mm], "startDerivative": vector(9.37, 7.69) * mm, "endDerivative": vector(8.97, 7.22) * mm});
            skLineSegment(sketch, "E202", {"start": v(41.22, -30.32) * mm, "end": v(49.66, -36.68) * mm});
            skFitSpline(sketch, "E203", {"points": [v(57.38, -4.34) * mm, v(59.33, -4.95) * mm, v(59.63, -7.08) * mm, v(58.1, -8.37) * mm, v(55.93, -9.17) * mm, v(54.25, -10.86) * mm, v(52.96, -13.66) * mm, v(53.2, -17.05) * mm, v(53.92, -19.3) * mm, v(52.32, -17.7) * mm, v(51.1, -15.44) * mm, v(50.6, -12.92) * mm, v(50.77, -10.19) * mm, v(52.42, -7.06) * mm, v(54.98, -5.07) * mm, v(57.38, -4.34) * mm]});
            skLineSegment(sketch, "E204", {"start": v(54.24, -20.39) * mm, "end": v(55.28, -24.22) * mm});
            skFitSpline(sketch, "E205", {"points": [v(55.28, -24.22) * mm, v(51.98, -23.12) * mm, v(49.25, -20.79) * mm, v(48.04, -18.14) * mm, v(48.28, -14.92) * mm, v(49.17, -12.42) * mm, v(49.33, -15.4) * mm, v(51.18, -19.3) * mm, v(54.24, -20.39) * mm], "startDerivative": vector(-26.72, 2.82) * mm, "endDerivative": vector(26.5, -4.82) * mm});
            skFitSpline(sketch, "E206", {"points": [v(40.4, -22.17) * mm, v(42.92, -20.39) * mm, v(45.02, -18.53) * mm, v(46.64, -16.36) * mm, v(47.15, -15.38) * mm], "startDerivative": vector(9.15, 6.43) * mm, "endDerivative": vector(2.95, 4.9) * mm});
            skFitSpline(sketch, "E207", {"points": [v(47.15, -15.38) * mm, v(47.15, -17.12) * mm, v(47.15, -18.86) * mm, v(47.96, -20.79) * mm, v(49.25, -22.25) * mm, v(50.73, -23.43) * mm], "startDerivative": vector(-0.08, -8.83) * mm, "endDerivative": vector(7.51, -5.69) * mm});
            skLineSegment(sketch, "E208", {"start": v(40.4, -22.17) * mm, "end": v(50.73, -23.43) * mm});
            skLineSegment(sketch, "E209", {"start": v(48.9, -24.22) * mm, "end": v(54.06, -24.92) * mm});
            skFitSpline(sketch, "E210", {"points": [v(54.06, -24.92) * mm, v(53.1, -29.22) * mm, v(51.77, -32.57) * mm, v(49.95, -35.34) * mm], "startDerivative": vector(-2.37, -12.3) * mm, "endDerivative": vector(-6.16, -8.6) * mm});
            skFitSpline(sketch, "E211", {"points": [v(48.9, -24.22) * mm, v(48.9, -28.65) * mm, v(49.95, -35.34) * mm], "startDerivative": vector(-0.44, -10.09) * mm, "endDerivative": vector(2.46, -12.83) * mm});
            skFitSpline(sketch, "E212", {"points": [v(40.58, -23.3) * mm, v(41.35, -26.92) * mm, v(42.58, -29.41) * mm, v(44.5, -30.94) * mm, v(46.7, -31.06) * mm, v(47.96, -29.32) * mm, v(47.96, -27.83) * mm, v(46.31, -25.73) * mm, v(41.35, -24.22) * mm, v(40.58, -23.3) * mm]});
            skSolve(sketch);
        }
        {
            var Q0;
            Q0 = qSketchRegion(id + "F10", true);
            extrude(context, id + "F11", {"entities" : qUnion([Q0]), "operationType" : NewBodyOperationType.ADD, "depth" : 2.8 * mm});
        }
        {
            var Q0;
            {var subQ0=sQuery(id+"F2.wireOp",EDGE,"E6");var subQ1=sQuery(id+"F2.wireOp",EDGE,"E5");var subQ2=sQuery(id+"F0.wireOp",EDGE,"E0");var subQ3=sQuery(id+"F2.wireOp",EDGE,"E12");var subQ4=sQuery(id+"F2.wireOp",EDGE,"E4");var subQ5=sQuery(id+"F2.wireOp",EDGE,"E2");var subQ6=sQuery(id+"F2.wireOp",EDGE,"E11");var subQ8=sQuery(id+"F2.wireOp",EDGE,"E7");var subQ11=sQuery(id+"F2.wireOp",EDGE,"E8");var subQ12=sQuery(id+"F2.wireOp",EDGE,"E3");var subQ14=sQuery(id+"F2.wireOp",EDGE,"E13");var subQ15=sQuery(id+"F2.wireOp",EDGE,"E1.0.0");var subQ16=sQuery(id+"F2.wireOp",EDGE,"E9");var subQ17=sQuery(id+"F2.wireOp",EDGE,"E10");Q0=makeQuery(id+"F5.boolean.opBoolean","SPLIT",FACE,{"disambiguationData":[TD([makeQuery(id+"F1.opExtrude","SWEPT_FACE",FACE,{"disambiguationData":[OSD([subQ2])]})])],"derivedFrom":makeQuery(id+"F3.boolean.opBoolean","MERGE",FACE,{"derivedFrom":[makeQuery(id+"F1.opExtrude","CAP_FACE",FACE,{"disambiguationData":[OSD([subQ2])],"isStart":true}),makeQuery(id+"F3.opExtrude","CAP_FACE",FACE,{"disambiguationData":[OSD([subQ15,subQ1,subQ0,subQ8,subQ6])],"isStart":true}),makeQuery(id+"F3.opExtrude","CAP_FACE",FACE,{"disambiguationData":[OSD([subQ15,subQ5,subQ12,subQ4,subQ6])],"isStart":true}),makeQuery(id+"F3.opExtrude","CAP_FACE",FACE,{"disambiguationData":[OSD([subQ15,subQ11,subQ16,subQ17,subQ6])],"isStart":true}),makeQuery(id+"F3.opExtrude","CAP_FACE",FACE,{"disambiguationData":[OSD([subQ15,subQ3,subQ14])],"isStart":true})]})});}
            var sketch = newSketch(context, id + "F12", { "sketchPlane" : qUnion([Q0])});
            skCircle(sketch, "E213", {"center": v(41.25, -45) * mm, "radius": 2.74 * mm});
            skCircle(sketch, "E214", {"center": v(30.45, -25.04) * mm, "radius": 2.71 * mm});
            skCircle(sketch, "E215", {"center": v(68.61, -2.65) * mm, "radius": 1.18 * mm});
            skCircle(sketch, "E216", {"center": v(66.8, 6.27) * mm, "radius": 1.39 * mm});
            skCircle(sketch, "E217", {"center": v(-44.18, -47.84) * mm, "radius": 2.16 * mm});
            skCircle(sketch, "E218", {"center": v(-50.45, -40.28) * mm, "radius": 1.94 * mm});
            skCircle(sketch, "E219", {"center": v(-17.96, -44.79) * mm, "radius": 1.66 * mm});
            skCircle(sketch, "E220", {"center": v(-64.35, -4.37) * mm, "radius": 0.8 * mm});
            skSolve(sketch);
        }
        {
            var Q0;
            Q0 = qSketchRegion(id + "F12", true);
            extrude(context, id + "F13", {"entities" : qUnion([Q0]), "operationType" : NewBodyOperationType.ADD, "depth" : 5.08 * mm});
        }
        {
            var Q0;
            {var subQ0=sQuery(id+"F2.wireOp",EDGE,"E1.0.0");var subQ1=sQuery(id+"F2.wireOp",EDGE,"E11");Q0=makeQuery(id+"F3.boolean.opBoolean","MERGE",FACE,{"derivedFrom":[makeQuery(id+"F1.opExtrude","CAP_FACE",FACE,{"disambiguationData":[OSD([sQuery(id+"F0.wireOp",EDGE,"E0")])],"isStart":false}),makeQuery(id+"F3.opExtrude","CAP_FACE",FACE,{"disambiguationData":[OSD([subQ0,sQuery(id+"F2.wireOp",EDGE,"E5"),sQuery(id+"F2.wireOp",EDGE,"E6"),sQuery(id+"F2.wireOp",EDGE,"E7"),subQ1])],"isStart":false}),makeQuery(id+"F3.opExtrude","CAP_FACE",FACE,{"disambiguationData":[OSD([subQ0,sQuery(id+"F2.wireOp",EDGE,"E2"),sQuery(id+"F2.wireOp",EDGE,"E3"),sQuery(id+"F2.wireOp",EDGE,"E4"),subQ1])],"isStart":false}),makeQuery(id+"F3.opExtrude","CAP_FACE",FACE,{"disambiguationData":[OSD([subQ0,sQuery(id+"F2.wireOp",EDGE,"E8"),sQuery(id+"F2.wireOp",EDGE,"E9"),sQuery(id+"F2.wireOp",EDGE,"E10"),subQ1])],"isStart":false}),makeQuery(id+"F3.opExtrude","CAP_FACE",FACE,{"disambiguationData":[OSD([subQ0,sQuery(id+"F2.wireOp",EDGE,"E12"),sQuery(id+"F2.wireOp",EDGE,"E13")])],"isStart":false})]});}
            var sketch = newSketch(context, id + "F14", { "sketchPlane" : qUnion([Q0])});
            skCircle(sketch, "E221", {"center": v(-40.93, 0.24) * mm, "radius": 3.35 * mm});
            skCircle(sketch, "E222", {"center": v(-54.32, -26.35) * mm, "radius": 2.82 * mm});
            skCircle(sketch, "E223", {"center": v(-6.88, -36.48) * mm, "radius": 2.84 * mm});
            skCircle(sketch, "E224", {"center": v(9.76, -40.31) * mm, "radius": 1.62 * mm});
            skCircle(sketch, "E225", {"center": v(46.88, -47.77) * mm, "radius": 3.77 * mm});
            skCircle(sketch, "E226", {"center": v(64.11, -4.78) * mm, "radius": 1.3 * mm});
            skCircle(sketch, "E227", {"center": v(-69.19, -1.6) * mm, "radius": 1.65 * mm});
            skCircle(sketch, "E228", {"center": v(-38.36, -42.18) * mm, "radius": 1.82 * mm});
            skCircle(sketch, "E229", {"center": v(-33.21, -38.15) * mm, "radius": 2.64 * mm});
            skCircle(sketch, "E230", {"center": v(-28.38, -32.04) * mm, "radius": 3.98 * mm});
            skCircle(sketch, "E231", {"center": v(-43.34, -43.78) * mm, "radius": 0.94 * mm});
            skSolve(sketch);
        }
        {
            var Q0;
            Q0 = qSketchRegion(id + "F14", true);
            extrude(context, id + "F15", {"entities" : qUnion([Q0]), "operationType" : NewBodyOperationType.ADD, "depth" : 5.08 * mm});
        }
        {
            var Q0;
            Q0=qCreatedBy(makeId("Top.planeOp"),FACE);
            var sketch = newSketch(context, id + "F16", { "sketchPlane" : qUnion([Q0])});
            skLineSegment(sketch, "E232.bottom", {"start": v(-50.98, 21.39) * mm, "end": v(50.8, 21.39) * mm});
            skLineSegment(sketch, "E232.top", {"start": v(-50.98, -21.39) * mm, "end": v(50.8, -21.39) * mm});
            skLineSegment(sketch, "E232.left", {"start": v(-50.98, 21.39) * mm, "end": v(-50.98, -21.39) * mm});
            skLineSegment(sketch, "E232.right", {"start": v(50.8, 21.39) * mm, "end": v(50.8, -21.39) * mm});
            skSolve(sketch);
        }
        {
            var Q0;
            Q0 = qSketchRegion(id + "F16", true);
            extrude(context, id + "F17", {"entities" : qUnion([Q0]), "operationType" : NewBodyOperationType.REMOVE, "oppositeDirection" : true, "depth" : 38.1 * mm});
        }
    });
